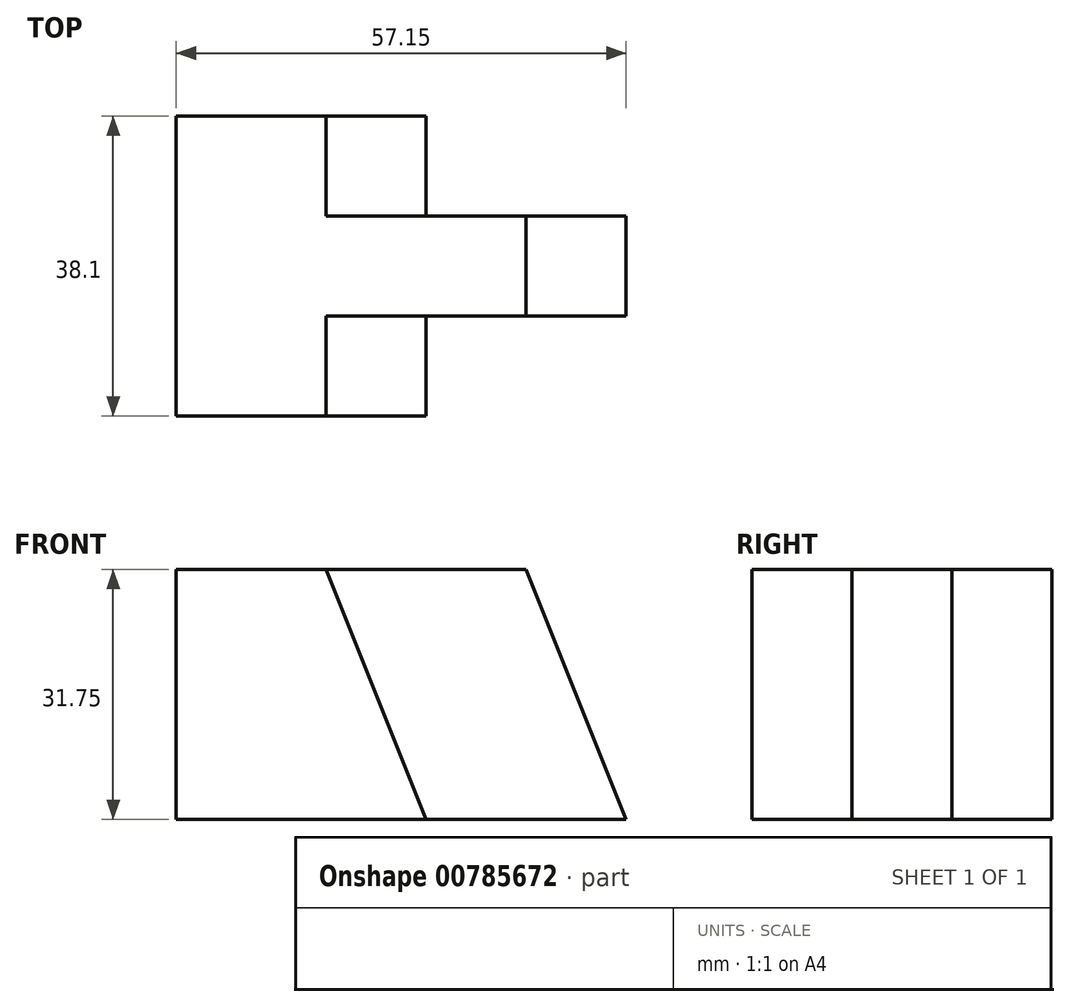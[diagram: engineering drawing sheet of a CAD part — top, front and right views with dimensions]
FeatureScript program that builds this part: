
annotation { "Feature Type Name" : "Feature", "Feature Type Description" : "" }
export const myFeature = defineFeature(function(context is Context, id is Id, definition is map)
    precondition{}
    {
        {
            var Q0;
            Q0=qCreatedBy(makeId("Front.planeOp"),FACE);
            var sketch = newSketch(context, id + "F0", { "sketchPlane" : qUnion([Q0])});
            skLineSegment(sketch, "E0", {"start": v(0, 0) * mm, "end": v(-57.15, 0) * mm});
            skLineSegment(sketch, "E1", {"start": v(-57.15, 0) * mm, "end": v(-57.15, 31.75) * mm});
            skLineSegment(sketch, "E2", {"start": v(-57.15, 31.75) * mm, "end": v(0, 31.75) * mm});
            skLineSegment(sketch, "E3", {"start": v(0, 31.75) * mm, "end": v(0, 0) * mm});
            skSolve(sketch);
        }
        {
            var Q0;
            Q0 = qSketchRegion(id + "F0", true);
            extrude(context, id + "F1", {"entities" : qUnion([Q0]), "depth" : 38.1 * mm, "offsetDistance" : 25.4 * mm});
        }
        {
            var Q0;
            Q0=makeQuery(id+"F1.opExtrude","CAP_FACE",FACE,{"disambiguationData":[OSD([sQuery(id+"F0.wireOp",EDGE,"E0"),sQuery(id+"F0.wireOp",EDGE,"E1"),sQuery(id+"F0.wireOp",EDGE,"E2"),sQuery(id+"F0.wireOp",EDGE,"E3")])],"isStart":false});
            var sketch = newSketch(context, id + "F2", { "sketchPlane" : qUnion([Q0])});
            skLineSegment(sketch, "E4", {"start": v(-57.15, 0) * mm, "end": v(-25.4, 0) * mm});
            skLineSegment(sketch, "E5", {"start": v(-57.15, 0) * mm, "end": v(-57.15, 31.75) * mm});
            skLineSegment(sketch, "E6", {"start": v(-57.15, 31.75) * mm, "end": v(-38.1, 31.75) * mm});
            skLineSegment(sketch, "E7", {"start": v(-38.1, 31.75) * mm, "end": v(-25.4, 0) * mm});
            skSolve(sketch);
        }
        {
            var Q0;
            {var subQ0=sQuery(id+"F2.wireOp",EDGE,"E7");Q0=makeQuery(id+"F2.imprint","IMPRINT",FACE,{"disambiguationData":[TD([[makeQuery(id+"F2.imprint","IMPRINT",EDGE,{"derivedFrom":subQ0}),1.0]])]});}
            extrude(context, id + "F3", {"entities" : qUnion([Q0]), "operationType" : NewBodyOperationType.REMOVE, "oppositeDirection" : true, "depth" : 12.7 * mm, "offsetDistance" : 25.4 * mm});
        }
        {
            var Q0;
            Q0=makeQuery(id+"F3.boolean.opBoolean","COPY",FACE,{"derivedFrom":makeQuery(id+"F3.opExtrude","CAP_FACE",FACE,{"disambiguationData":[OSD([sQuery(id+"F0.wireOp",EDGE,"E0"),sQuery(id+"F0.wireOp",EDGE,"E2"),sQuery(id+"F0.wireOp",EDGE,"E3"),sQuery(id+"F2.wireOp",EDGE,"E7")])],"isStart":false})});
            var sketch = newSketch(context, id + "F4", { "sketchPlane" : qUnion([Q0])});
            skLineSegment(sketch, "E8", {"start": v(-38.1, 31.75) * mm, "end": v(-12.7, 31.75) * mm});
            skLineSegment(sketch, "E9", {"start": v(-12.7, 31.75) * mm, "end": v(0, 0) * mm});
            skLineSegment(sketch, "E10", {"start": v(0, 0) * mm, "end": v(-25.4, 0) * mm});
            skLineSegment(sketch, "E11", {"start": v(-25.4, 0) * mm, "end": v(-38.1, 31.75) * mm});
            skSolve(sketch);
        }
        {
            var Q0;
            {var subQ0=sQuery(id+"F4.wireOp",EDGE,"E9");Q0=makeQuery(id+"F4.imprint","IMPRINT",FACE,{"disambiguationData":[TD([[makeQuery(id+"F4.imprint","IMPRINT",EDGE,{"derivedFrom":subQ0}),1.0]])]});}
            extrude(context, id + "F5", {"entities" : qUnion([Q0]), "operationType" : NewBodyOperationType.REMOVE, "oppositeDirection" : true, "depth" : 12.7 * mm, "offsetDistance" : 25.4 * mm});
        }
        {
            var Q0;
            Q0=makeQuery(id+"F1.opExtrude","CAP_FACE",FACE,{"disambiguationData":[OSD([sQuery(id+"F0.wireOp",EDGE,"E0"),sQuery(id+"F0.wireOp",EDGE,"E1"),sQuery(id+"F0.wireOp",EDGE,"E2"),sQuery(id+"F0.wireOp",EDGE,"E3")])],"isStart":true});
            var sketch = newSketch(context, id + "F6", { "sketchPlane" : qUnion([Q0])});
            skLineSegment(sketch, "E12", {"start": v(57.15, 0) * mm, "end": v(25.4, 0) * mm});
            skLineSegment(sketch, "E13", {"start": v(57.15, 0) * mm, "end": v(57.15, 31.75) * mm});
            skLineSegment(sketch, "E14", {"start": v(57.15, 31.75) * mm, "end": v(38.1, 31.75) * mm});
            skLineSegment(sketch, "E15", {"start": v(38.1, 31.75) * mm, "end": v(25.4, 0) * mm});
            skSolve(sketch);
        }
        {
            var Q0;
            {var subQ0=sQuery(id+"F6.wireOp",EDGE,"E15");Q0=makeQuery(id+"F6.imprint","IMPRINT",FACE,{"disambiguationData":[TD([[makeQuery(id+"F6.imprint","IMPRINT",EDGE,{"derivedFrom":subQ0}),-1.0]])]});}
            extrude(context, id + "F7", {"entities" : qUnion([Q0]), "operationType" : NewBodyOperationType.REMOVE, "oppositeDirection" : true, "depth" : 12.7 * mm, "offsetDistance" : 25.4 * mm});
        }
    });
